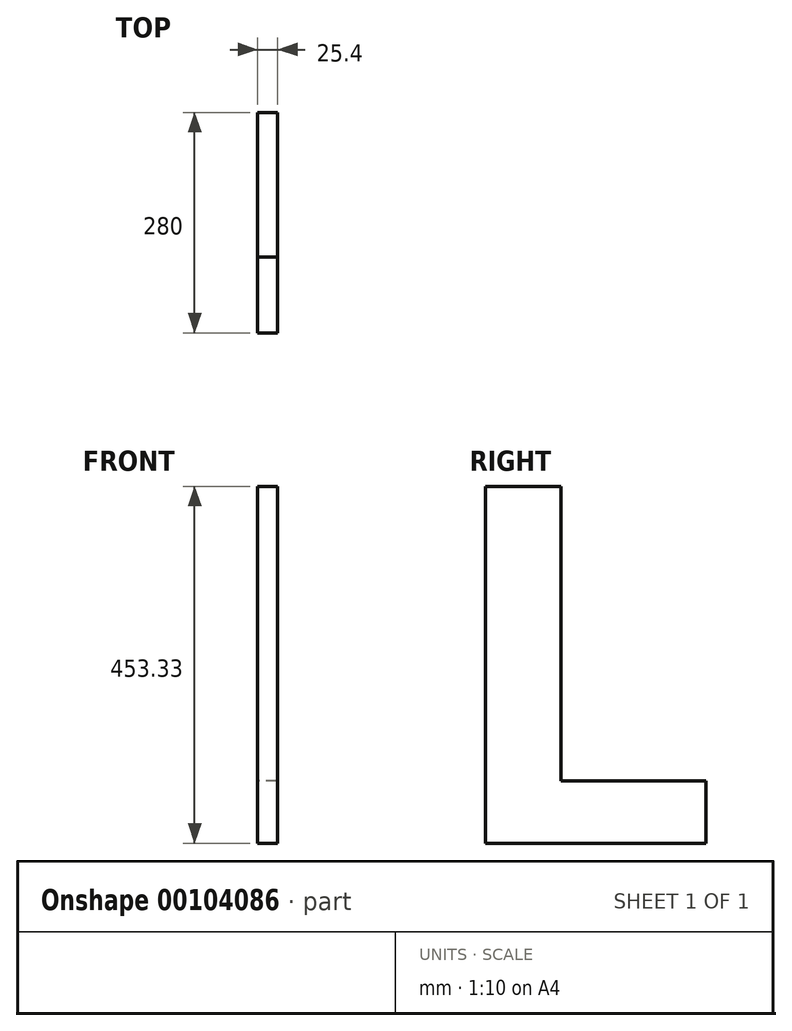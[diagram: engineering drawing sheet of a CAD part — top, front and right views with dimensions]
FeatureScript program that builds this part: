
annotation { "Feature Type Name" : "Feature", "Feature Type Description" : "" }
export const myFeature = defineFeature(function(context is Context, id is Id, definition is map)
    precondition{}
    {
        {
            var Q0;
            Q0=qCreatedBy(makeId("Right.planeOp"),FACE);
            var sketch = newSketch(context, id + "F0", { "sketchPlane" : qUnion([Q0])});
            skText(sketch, "E0", { "text": "L", "fontName": "OpenSans-Bold.ttf"});
            const initialGuessF0  = {"E0": [-0.22945, -0.22604, 1, 0, 0.4572]};
            skSetInitialGuess(sketch, initialGuessF0);
            skSolve(sketch);
        }
        {
            var Q0;
            Q0=makeQuery(id+"F0.imprint","IMPRINT",FACE,{"disambiguationData":[TD([[makeQuery(id+"F0.imprint","IMPRINT",EDGE,{"derivedFrom":sQuery(id+"F0.wireOp",EDGE,"E0.sketch_text.stroke-0")}),-1.0]])]});
            extrude(context, id + "F1", {"entities" : qUnion([Q0]), "endBound" : BoundingType.SYMMETRIC, "depth" : 25.4 * mm});
        }
    });
